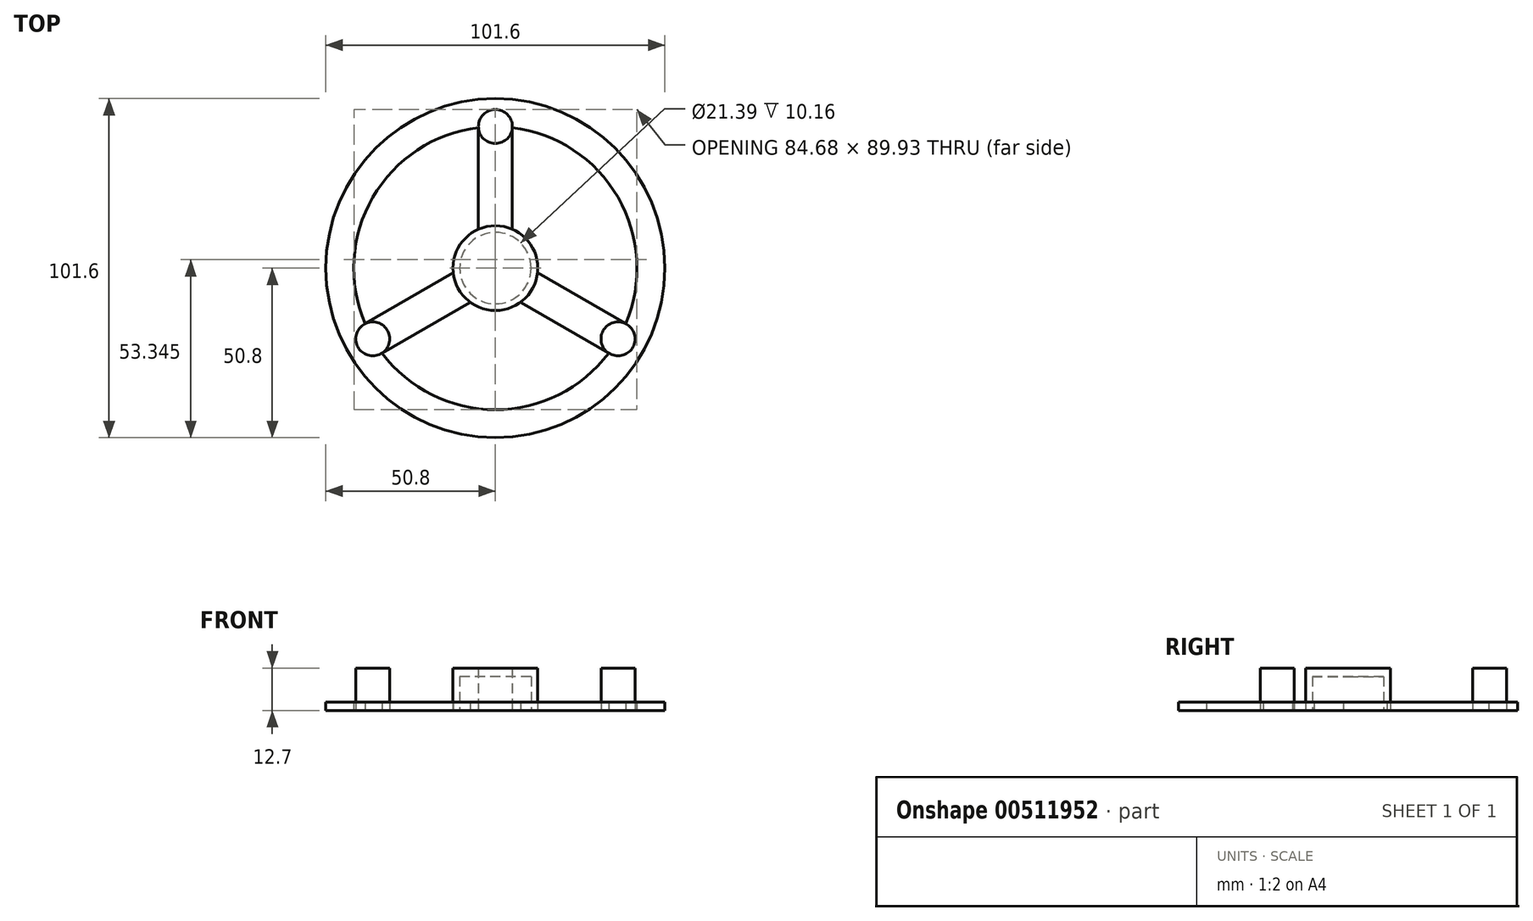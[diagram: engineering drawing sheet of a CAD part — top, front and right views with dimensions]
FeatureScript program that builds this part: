
annotation { "Feature Type Name" : "Feature", "Feature Type Description" : "" }
export const myFeature = defineFeature(function(context is Context, id is Id, definition is map)
    precondition{}
    {
        {
            var Q0;
            Q0=qCreatedBy(makeId("Top.planeOp"),FACE);
            var sketch = newSketch(context, id + "F0", { "sketchPlane" : qUnion([Q0])});
            skCircle(sketch, "E0", {"center": v(0, 0) * mm, "radius": 50.8 * mm});
            skCircle(sketch, "E1", {"center": v(0, 0) * mm, "radius": 42.42 * mm, "construction": true});
            skCircle(sketch, "E2", {"center": v(0, 0) * mm, "radius": 12.7 * mm, "construction": true});
            skLineSegment(sketch, "E3", {"start": v(0, 0) * mm, "end": v(0, 42.42) * mm, "construction": true});
            skLineSegment(sketch, "E4", {"start": v(0, 42.42) * mm, "end": v(0, 0) * mm, "construction": true});
            skLineSegment(sketch, "E5", {"start": v(-36.74, -21.2) * mm, "end": v(0, 0) * mm, "construction": true});
            skLineSegment(sketch, "E6", {"start": v(0, 0) * mm, "end": v(36.74, -21.2) * mm, "construction": true});
            skLineSegment(sketch, "E7", {"start": v(-5.08, 11.64) * mm, "end": v(-5.08, 42.11) * mm});
            skLineSegment(sketch, "E8", {"start": v(5.08, 42.11) * mm, "end": v(5.08, 11.64) * mm});
            skLineSegment(sketch, "E9", {"start": v(12.62, -1.42) * mm, "end": v(39.01, -16.66) * mm});
            skLineSegment(sketch, "E10", {"start": v(33.93, -25.46) * mm, "end": v(7.54, -10.22) * mm});
            skLineSegment(sketch, "E11", {"start": v(-7.54, -10.22) * mm, "end": v(-33.93, -25.46) * mm});
            skLineSegment(sketch, "E12", {"start": v(-12.62, -1.42) * mm, "end": v(-39.01, -16.66) * mm});
            skArc(sketch, "E13", {"start": v(-5.08, 11.64) * mm, "mid": v(-11, 6.35) * mm, "end": v(-12.62, -1.42) * mm});
            skArc(sketch, "E14", {"start": v(12.62, -1.42) * mm, "mid": v(11, 6.35) * mm, "end": v(5.08, 11.64) * mm});
            skArc(sketch, "E15", {"start": v(-7.54, -10.22) * mm, "mid": v(0, -12.7) * mm, "end": v(7.54, -10.22) * mm});
            skArc(sketch, "E16", {"start": v(-5.08, 42.11) * mm, "mid": v(-36.74, 21.2) * mm, "end": v(-39.01, -16.66) * mm});
            skArc(sketch, "E17", {"start": v(39.01, -16.66) * mm, "mid": v(36.74, 21.2) * mm, "end": v(5.08, 42.11) * mm});
            skArc(sketch, "E18", {"start": v(-33.93, -25.46) * mm, "mid": v(0, -42.42) * mm, "end": v(33.93, -25.46) * mm});
            skCircle(sketch, "E19", {"center": v(0, 0) * mm, "radius": 12.7 * mm});
            skCircle(sketch, "E20", {"center": v(-36.74, -21.2) * mm, "radius": 5.09 * mm});
            skCircle(sketch, "E21", {"center": v(36.74, -21.2) * mm, "radius": 5.09 * mm});
            skCircle(sketch, "E22", {"center": v(0, 42.42) * mm, "radius": 5.09 * mm});
            skSolve(sketch);
        }
        {
            var Q0;
            {var subQ0=sQuery(id+"F0.wireOp",EDGE,"E11");Q0=makeQuery(id+"F0.imprint","IMPRINT",FACE,{"disambiguationData":[TD([[makeQuery(id+"F0.imprint","IMPRINT",EDGE,{"derivedFrom":subQ0}),-1.0]])]});}
            var Q1;
            Q1=makeQuery(id+"F0.imprint","IMPRINT",FACE,{"disambiguationData":[TD([[makeQuery(id+"F0.imprint","IMPRINT",EDGE,{"derivedFrom":sQuery(id+"F0.wireOp",EDGE,"E0")}),1.0]])]});
            var Q2;
            {var subQ0=sQuery(id+"F0.wireOp",EDGE,"E9");Q2=makeQuery(id+"F0.imprint","IMPRINT",FACE,{"disambiguationData":[TD([[makeQuery(id+"F0.imprint","IMPRINT",EDGE,{"derivedFrom":subQ0}),-1.0]])]});}
            var Q3;
            {var subQ0=sQuery(id+"F0.wireOp",EDGE,"E7");Q3=makeQuery(id+"F0.imprint","IMPRINT",FACE,{"disambiguationData":[TD([[makeQuery(id+"F0.imprint","IMPRINT",EDGE,{"derivedFrom":subQ0}),-1.0]])]});}
            extrude(context, id + "F1", {"entities" : qUnion([Q0, Q1, Q2, Q3]), "depth" : 2.54 * mm});
        }
        {
            var Q0;
            {var subQ0=sQuery(id+"F0.wireOp",EDGE,"E19");var subQ4=makeQuery(id+"F0.imprint","INTERSECT",VERTEX,{"derivedFrom":[sQuery(id+"F0.wireOp",EDGE,"E7"),subQ0]});Q0=makeQuery(id+"F0.imprint","IMPRINT",FACE,{"disambiguationData":[TD([[makeQuery(id+"F0.imprint","IMPRINT",EDGE,{"disambiguationData":[TD([[subQ4,1.0]])],"derivedFrom":subQ0}),1.0]])]});}
            var Q1;
            {var subQ0=sQuery(id+"F0.wireOp",EDGE,"E20");var subQ1=makeQuery(id+"F0.imprint","INTERSECT",VERTEX,{"derivedFrom":[sQuery(id+"F0.wireOp",EDGE,"E11"),sQuery(id+"F0.wireOp",EDGE,"E18"),subQ0]});Q1=makeQuery(id+"F0.imprint","IMPRINT",FACE,{"disambiguationData":[TD([[makeQuery(id+"F0.imprint","IMPRINT",EDGE,{"disambiguationData":[TD([[subQ1,1.0]])],"derivedFrom":subQ0}),1.0]])]});}
            var Q2;
            {var subQ0=sQuery(id+"F0.wireOp",EDGE,"E21");var subQ1=makeQuery(id+"F0.imprint","INTERSECT",VERTEX,{"derivedFrom":[sQuery(id+"F0.wireOp",EDGE,"E9"),sQuery(id+"F0.wireOp",EDGE,"E17"),subQ0]});Q2=makeQuery(id+"F0.imprint","IMPRINT",FACE,{"disambiguationData":[TD([[makeQuery(id+"F0.imprint","IMPRINT",EDGE,{"disambiguationData":[TD([[subQ1,-1.0]])],"derivedFrom":subQ0}),1.0]])]});}
            var Q3;
            {var subQ0=sQuery(id+"F0.wireOp",EDGE,"E22");var subQ1=makeQuery(id+"F0.imprint","INTERSECT",VERTEX,{"derivedFrom":[sQuery(id+"F0.wireOp",EDGE,"E7"),sQuery(id+"F0.wireOp",EDGE,"E16"),subQ0]});Q3=makeQuery(id+"F0.imprint","IMPRINT",FACE,{"disambiguationData":[TD([[makeQuery(id+"F0.imprint","IMPRINT",EDGE,{"disambiguationData":[TD([[subQ1,-1.0]])],"derivedFrom":subQ0}),1.0]])]});}
            extrude(context, id + "F2", {"entities" : qUnion([Q0, Q1, Q2, Q3]), "depth" : 12.7 * mm});
        }
        {
            var Q0;
            {var subQ0=sQuery(id+"F0.wireOp",EDGE,"E19");var subQ4=makeQuery(id+"F0.imprint","INTERSECT",VERTEX,{"derivedFrom":[sQuery(id+"F0.wireOp",EDGE,"E7"),subQ0]});Q0=makeQuery(id+"F0.imprint","IMPRINT",FACE,{"disambiguationData":[TD([[makeQuery(id+"F0.imprint","IMPRINT",EDGE,{"disambiguationData":[TD([[subQ4,1.0]])],"derivedFrom":subQ0}),1.0]])]});}
            var sketch = newSketch(context, id + "F3", { "sketchPlane" : qUnion([Q0])});
            skCircle(sketch, "E23", {"center": v(0, 0) * mm, "radius": 10.7 * mm});
            skSolve(sketch);
        }
        {
            var Q0;
            Q0=makeQuery(id+"F3.imprint","IMPRINT",FACE,{"disambiguationData":[TD([[makeQuery(id+"F3.imprint","IMPRINT",EDGE,{"derivedFrom":sQuery(id+"F3.wireOp",EDGE,"E23")}),1.0]])]});
            extrude(context, id + "F4", {"entities" : qUnion([Q0]), "operationType" : NewBodyOperationType.REMOVE, "depth" : 10.16 * mm});
        }
    });
